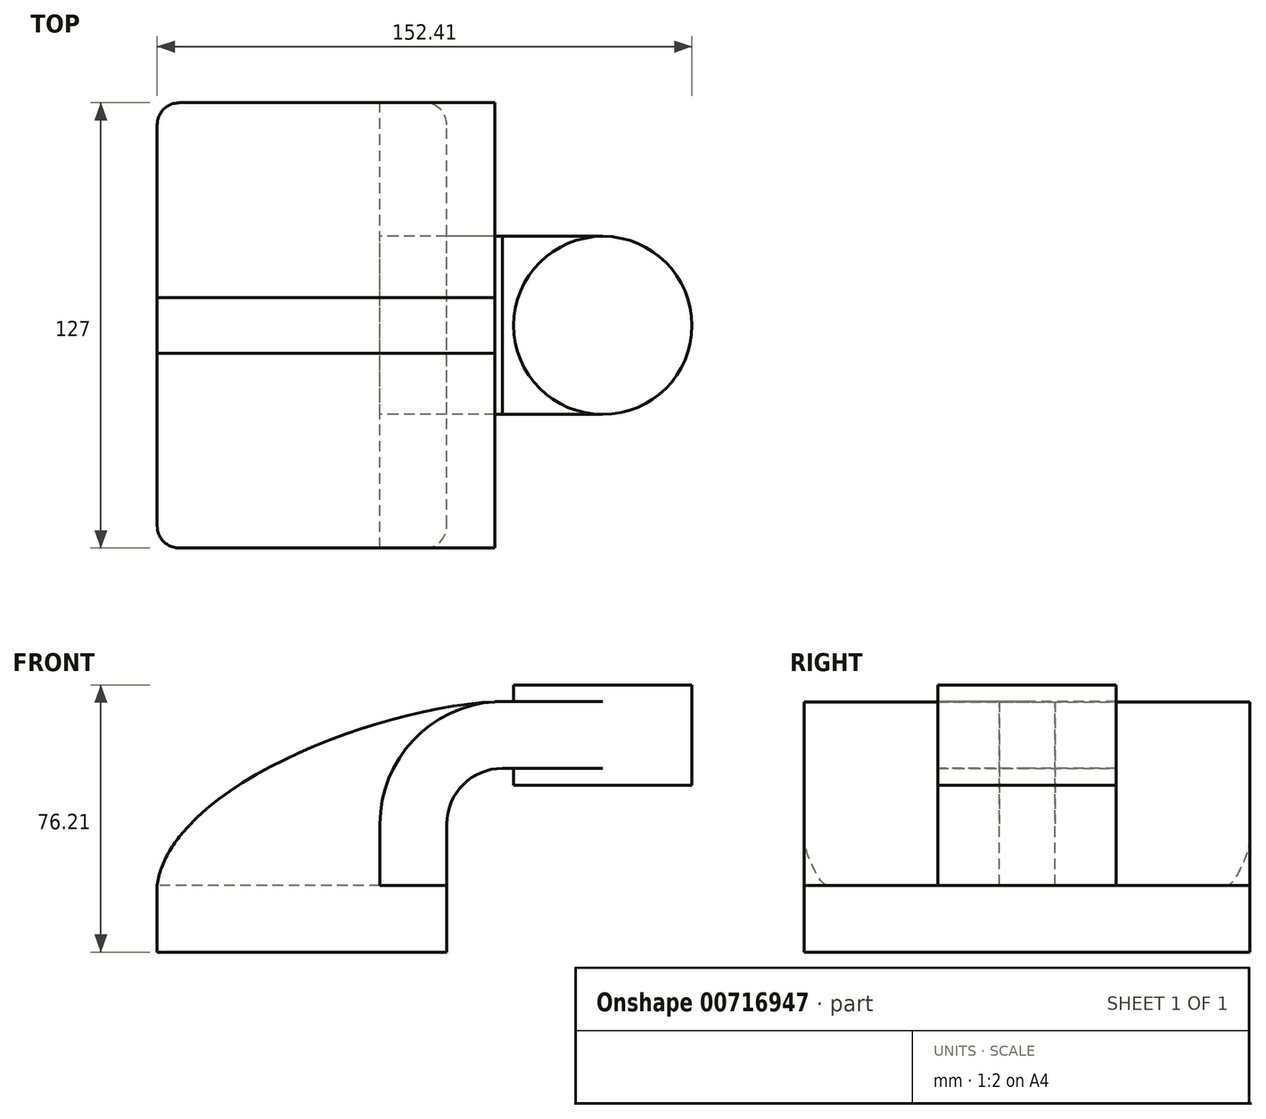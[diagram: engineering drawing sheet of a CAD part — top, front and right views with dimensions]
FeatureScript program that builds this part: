
annotation { "Feature Type Name" : "Feature", "Feature Type Description" : "" }
export const myFeature = defineFeature(function(context is Context, id is Id, definition is map)
    precondition{}
    {
        {
            var Q0;
            Q0=qCreatedBy(makeId("Front.planeOp"),FACE);
            var sketch = newSketch(context, id + "F0", { "sketchPlane" : qUnion([Q0])});
            skLineSegment(sketch, "E0.bottom", {"start": v(41.28, -9.52) * mm, "end": v(-41.28, -9.53) * mm});
            skLineSegment(sketch, "E0.top", {"start": v(41.28, 9.53) * mm, "end": v(-41.28, 9.53) * mm});
            skLineSegment(sketch, "E0.left", {"start": v(41.28, -9.52) * mm, "end": v(41.28, 9.53) * mm});
            skLineSegment(sketch, "E0.right", {"start": v(-41.28, -9.53) * mm, "end": v(-41.28, 9.53) * mm});
            skPoint(sketch, "E0.middle", {"position": v(0, 0) * mm});
            skLineSegment(sketch, "E1.bottom", {"start": v(111.12, 38.1) * mm, "end": v(60.33, 38.1) * mm});
            skLineSegment(sketch, "E1.top", {"start": v(111.12, 66.68) * mm, "end": v(60.33, 66.68) * mm});
            skLineSegment(sketch, "E1.left", {"start": v(111.12, 38.1) * mm, "end": v(111.12, 66.68) * mm});
            skLineSegment(sketch, "E1.right", {"start": v(60.33, 38.1) * mm, "end": v(60.33, 66.68) * mm});
            skPoint(sketch, "E1.middle", {"position": v(85.72, 52.39) * mm});
            skLineSegment(sketch, "E2", {"start": v(41.28, 9.53) * mm, "end": v(41.28, 27) * mm});
            skArc(sketch, "E3", {"start": v(41.27, 27) * mm, "mid": v(45.92, 38.23) * mm, "end": v(57.15, 42.88) * mm});
            skLineSegment(sketch, "E4", {"start": v(57.15, 42.88) * mm, "end": v(85.73, 42.88) * mm});
            skLineSegment(sketch, "E5.0", {"start": v(57.15, 61.93) * mm, "end": v(85.73, 61.93) * mm});
            skArc(sketch, "E5.1", {"start": v(22.22, 27) * mm, "mid": v(32.45, 51.7) * mm, "end": v(57.15, 61.93) * mm});
            skLineSegment(sketch, "E5.2", {"start": v(22.22, 9.53) * mm, "end": v(22.22, 27) * mm});
            skLineSegment(sketch, "E6", {"start": v(85.73, 38.1) * mm, "end": v(85.72, 66.68) * mm});
            skFitSpline(sketch, "E7", {"points": [v(-41.28, 9.53) * mm, v(57.15, 61.93) * mm], "startDerivative": vector(10.8, 84.96) * mm, "endDerivative": vector(101.1, 1.74) * mm});
            skSolve(sketch);
        }
        {
            var Q0;
            {var subQ0=sQuery(id+"F0.wireOp",EDGE,"E7");var subQ1=sQuery(id+"F0.wireOp",EDGE,"E5.1");var subQ3=makeQuery(id+"F0.imprint","INTERSECT",VERTEX,{"derivedFrom":[subQ1,subQ0]});Q0=makeQuery(id+"F0.imprint","IMPRINT",FACE,{"disambiguationData":[TD([[makeQuery(id+"F0.imprint","IMPRINT",EDGE,{"disambiguationData":[TD([[subQ3,-1.0]])],"derivedFrom":subQ1}),-1.0]])]});}
            var Q1;
            Q1=makeQuery(id+"F0.imprint","IMPRINT",FACE,{"disambiguationData":[TD([[makeQuery(id+"F0.imprint","IMPRINT",EDGE,{"derivedFrom":sQuery(id+"F0.wireOp",EDGE,"E0.bottom")}),-1.0]])]});
            extrude(context, id + "F1", {"entities" : qUnion([Q0, Q1]), "endBound" : BoundingType.SYMMETRIC, "depth" : 127 * mm, "offsetDistance" : 25.4 * mm});
        }
        {
            var Q0;
            {var subQ1=sQuery(id+"F0.wireOp",EDGE,"E2");Q0=makeQuery(id+"F0.imprint","IMPRINT",FACE,{"disambiguationData":[TD([[makeQuery(id+"F0.imprint","IMPRINT",EDGE,{"derivedFrom":subQ1}),1.0]])]});}
            var Q1;
            {var subQ0=sQuery(id+"F0.wireOp",EDGE,"E4");var subQ1=sQuery(id+"F0.wireOp",EDGE,"E1.right");var subQ2=makeQuery(id+"F0.imprint","INTERSECT",VERTEX,{"derivedFrom":[subQ1,subQ0]});Q1=makeQuery(id+"F0.imprint","IMPRINT",FACE,{"disambiguationData":[TD([[makeQuery(id+"F0.imprint","IMPRINT",EDGE,{"disambiguationData":[TD([[subQ2,-1.0]])],"derivedFrom":subQ1}),-1.0]])]});}
            extrude(context, id + "F2", {"entities" : qUnion([Q0, Q1]), "endBound" : BoundingType.SYMMETRIC, "depth" : 50.8 * mm, "offsetDistance" : 25.4 * mm});
        }
        {
            var Q0;
            {var subQ3=sQuery(id+"F0.wireOp",EDGE,"E5.2");Q0=makeQuery(id+"F0.imprint","IMPRINT",FACE,{"disambiguationData":[TD([[makeQuery(id+"F0.imprint","IMPRINT",EDGE,{"derivedFrom":subQ3}),1.0]])]});}
            extrude(context, id + "F3", {"entities" : qUnion([Q0]), "endBound" : BoundingType.SYMMETRIC, "depth" : 15.88 * mm, "offsetDistance" : 25.4 * mm});
        }
        {
            var Q0;
            {var subQ0=sQuery(id+"F0.wireOp",EDGE,"E1.left");Q0=makeQuery(id+"F0.imprint","IMPRINT",FACE,{"disambiguationData":[TD([[makeQuery(id+"F0.imprint","IMPRINT",EDGE,{"derivedFrom":subQ0}),1.0]])]});}
            var Q1;
            Q1=sQuery(id+"F0.wireOp",EDGE,"E6");
            revolve(context, id + "F4", {"operationType" : NewBodyOperationType.ADD, "surfaceOperationType" : NewSurfaceOperationType.NEW, "entities" : qUnion([Q0]), "axis" : qUnion([Q1]), "revolveType" : RevolveType.FULL});
        }
        {
            var Q0;
            Q0=makeQuery(id+"F1.opExtrude","CAP_EDGE",EDGE,{"disambiguationData":[OSD([sQuery(id+"F0.wireOp",EDGE,"E0.left")])],"isStart":false});
            var Q1;
            Q1=makeQuery(id+"F1.opExtrude","CAP_EDGE",EDGE,{"disambiguationData":[OSD([sQuery(id+"F0.wireOp",EDGE,"E0.left")])],"isStart":true});
            var Q2;
            Q2=makeQuery(id+"F1.opExtrude","CAP_EDGE",EDGE,{"disambiguationData":[OSD([sQuery(id+"F0.wireOp",EDGE,"E0.right")])],"isStart":true});
            var Q3;
            Q3=makeQuery(id+"F1.opExtrude","CAP_EDGE",EDGE,{"disambiguationData":[OSD([sQuery(id+"F0.wireOp",EDGE,"E0.right")])],"isStart":false});
            fillet(context, id + "F5", {"entities" : qUnion([Q0, Q1, Q2, Q3]), "radius" : 6.35 * mm, "tangentPropagation" : true, "allowEdgeOverflow" : false});
        }
    });
